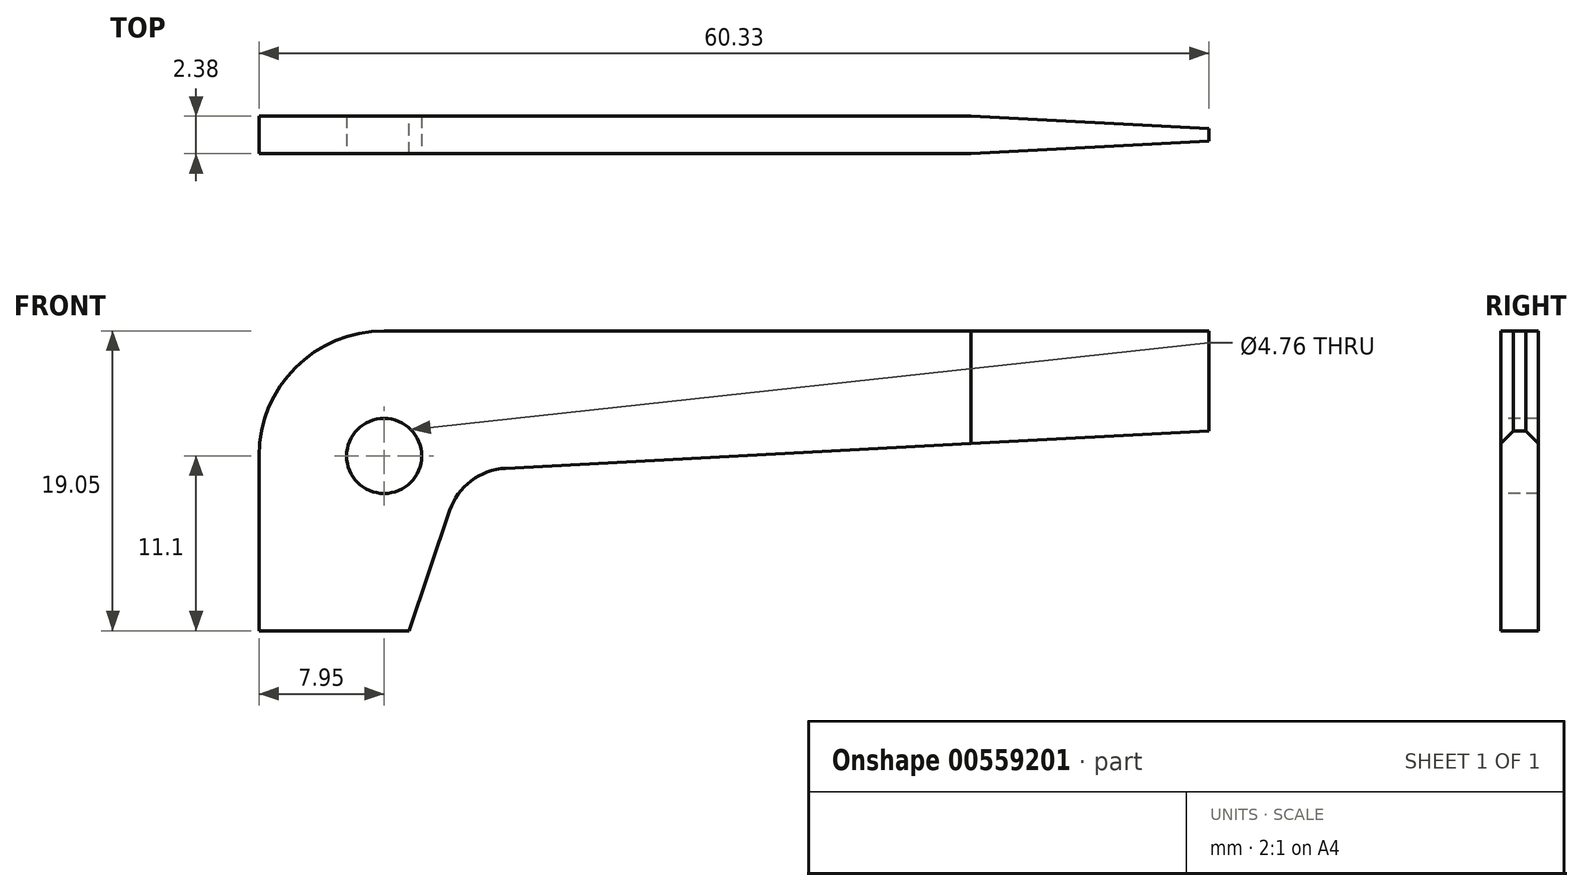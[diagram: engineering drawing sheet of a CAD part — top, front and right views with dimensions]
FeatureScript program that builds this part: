
annotation { "Feature Type Name" : "Feature", "Feature Type Description" : "" }
export const myFeature = defineFeature(function(context is Context, id is Id, definition is map)
    precondition{}
    {
        {
            var Q0;
            Q0=qCreatedBy(makeId("Front.planeOp"),FACE);
            var sketch = newSketch(context, id + "F0", { "sketchPlane" : qUnion([Q0])});
            skLineSegment(sketch, "E0.top", {"start": v(7.95, 19.05) * mm, "end": v(60.33, 19.05) * mm});
            skLineSegment(sketch, "E0.left", {"start": v(0, 0) * mm, "end": v(0, 11.1) * mm});
            skLineSegment(sketch, "E1", {"start": v(9.52, 0) * mm, "end": v(12.11, 7.63) * mm});
            skLineSegment(sketch, "E2", {"start": v(60.33, 12.7) * mm, "end": v(15.66, 10.32) * mm});
            skLineSegment(sketch, "E3", {"start": v(0, 0) * mm, "end": v(9.53, 0) * mm});
            skLineSegment(sketch, "E4", {"start": v(60.33, 19.05) * mm, "end": v(60.33, 12.7) * mm});
            skArc(sketch, "E5", {"start": v(15.66, 10.32) * mm, "mid": v(13.47, 9.52) * mm, "end": v(12.11, 7.63) * mm});
            skPoint(sketch, "E6.visualSharp", {"position": v(0, 19.05) * mm});
            skArc(sketch, "E6.filletArc", {"start": v(7.95, 19.05) * mm, "mid": v(2.33, 16.72) * mm, "end": v(0, 11.1) * mm});
            skSolve(sketch);
        }
        {
            var Q0;
            Q0 = qSketchRegion(id + "F0", true);
            extrude(context, id + "F1", {"entities" : qUnion([Q0]), "depth" : 2.38 * mm, "offsetDistance" : 25.4 * mm});
        }
        {
            var Q0;
            Q0=makeQuery(id+"F1.opExtrude","CAP_FACE",FACE,{"disambiguationData":[OSD([sQuery(id+"F0.wireOp",EDGE,"E0.top"),sQuery(id+"F0.wireOp",EDGE,"E0.left"),sQuery(id+"F0.wireOp",EDGE,"E1"),sQuery(id+"F0.wireOp",EDGE,"E2"),sQuery(id+"F0.wireOp",EDGE,"E3"),sQuery(id+"F0.wireOp",EDGE,"E4"),sQuery(id+"F0.wireOp",EDGE,"E5"),sQuery(id+"F0.wireOp",EDGE,"E6.filletArc")])],"isStart":false});
            var sketch = newSketch(context, id + "F2", { "sketchPlane" : qUnion([Q0])});
            skCircle(sketch, "E7", {"center": v(7.95, 11.1) * mm, "radius": 2.38 * mm});
            skSolve(sketch);
        }
        {
            var Q0;
            Q0=makeQuery(id+"F2.imprint","IMPRINT",FACE,{"disambiguationData":[TD([[makeQuery(id+"F2.imprint","IMPRINT",EDGE,{"derivedFrom":sQuery(id+"F2.wireOp",EDGE,"E7")}),1.0]])]});
            extrude(context, id + "F3", {"entities" : qUnion([Q0]), "operationType" : NewBodyOperationType.REMOVE, "oppositeDirection" : true, "depth" : 25.4 * mm, "offsetDistance" : 25.4 * mm});
        }
        {
            var Q0;
            Q0=makeQuery(id+"F1.opExtrude","SWEPT_FACE",FACE,{"disambiguationData":[OSD([sQuery(id+"F0.wireOp",EDGE,"E0.top")])]});
            var sketch = newSketch(context, id + "F4", { "sketchPlane" : qUnion([Q0])});
            skLineSegment(sketch, "E8", {"start": v(45.24, 0) * mm, "end": v(60.33, -0.8) * mm});
            skLineSegment(sketch, "E9", {"start": v(60.33, 0) * mm, "end": v(45.24, 0) * mm});
            skLineSegment(sketch, "E10.MirrorCS", {"start": v(45.24, -2.38) * mm, "end": v(60.33, -1.59) * mm});
            skLineSegment(sketch, "E11.MirrorCS", {"start": v(60.33, -2.38) * mm, "end": v(45.24, -2.38) * mm});
            skSolve(sketch);
        }
        {
            var Q0;
            {var subQ0=sQuery(id+"F4.wireOp",EDGE,"E8");Q0=makeQuery(id+"F4.imprint","IMPRINT",FACE,{"disambiguationData":[TD([[makeQuery(id+"F4.imprint","IMPRINT",EDGE,{"derivedFrom":subQ0}),1.0]])]});}
            var Q1;
            {var subQ0=sQuery(id+"F4.wireOp",EDGE,"E10.MirrorCS");Q1=makeQuery(id+"F4.imprint","IMPRINT",FACE,{"disambiguationData":[TD([[makeQuery(id+"F4.imprint","IMPRINT",EDGE,{"derivedFrom":subQ0}),-1.0]])]});}
            extrude(context, id + "F5", {"entities" : qUnion([Q0, Q1]), "operationType" : NewBodyOperationType.REMOVE, "oppositeDirection" : true, "depth" : 25.4 * mm, "offsetDistance" : 25.4 * mm});
        }
    });
